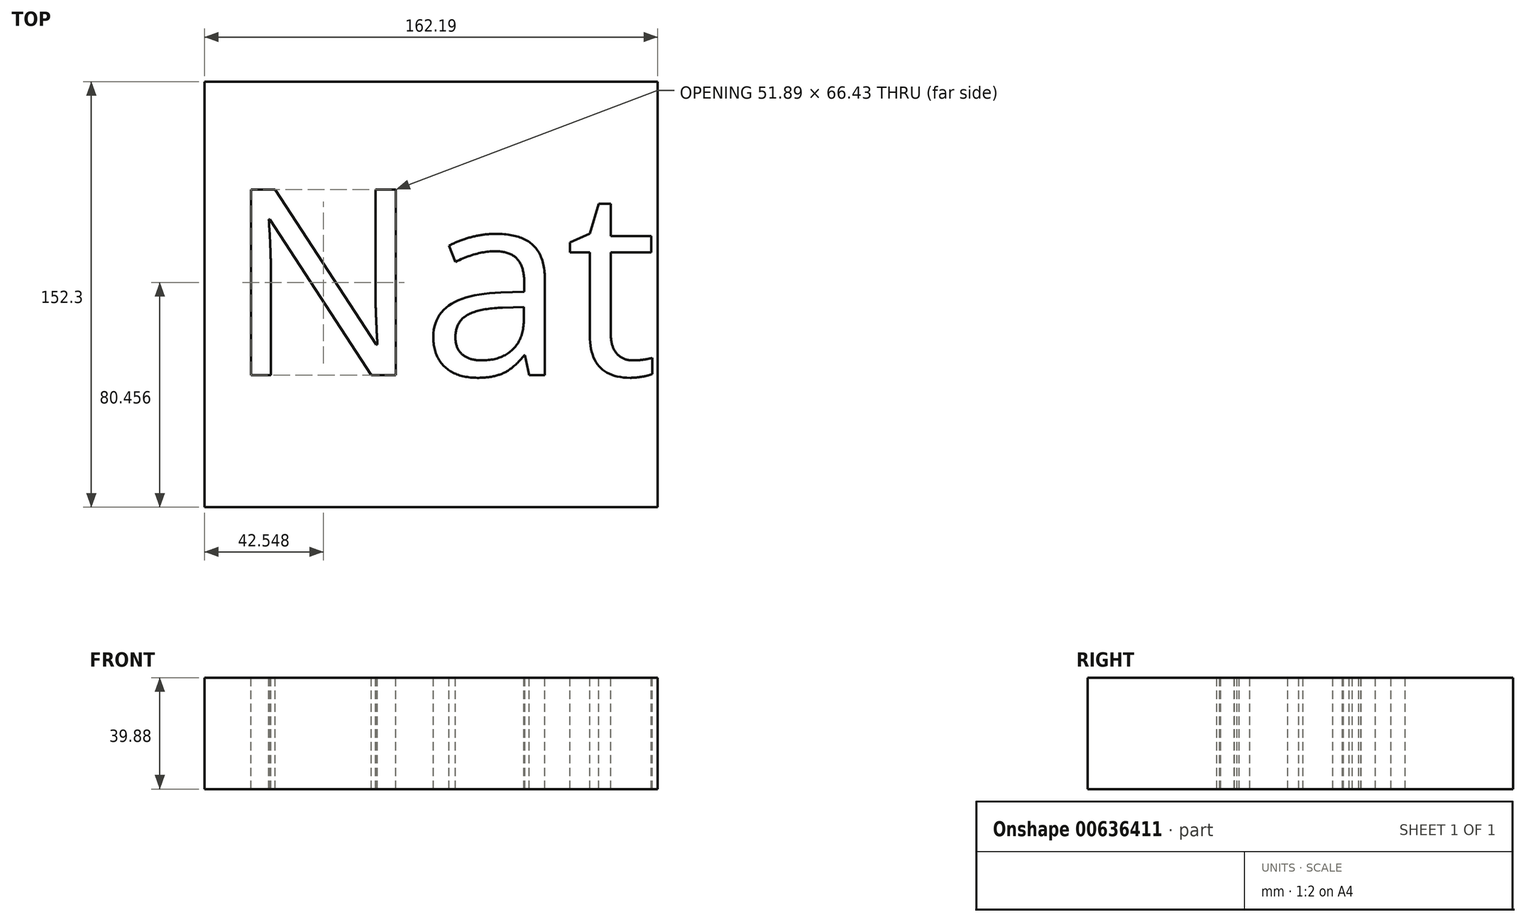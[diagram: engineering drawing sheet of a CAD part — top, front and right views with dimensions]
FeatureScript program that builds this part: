
annotation { "Feature Type Name" : "Feature", "Feature Type Description" : "" }
export const myFeature = defineFeature(function(context is Context, id is Id, definition is map)
    precondition{}
    {
        {
            var Q0;
            Q0=qCreatedBy(makeId("Top.planeOp"),FACE);
            var sketch = newSketch(context, id + "F0", { "sketchPlane" : qUnion([Q0])});
            skLineSegment(sketch, "E0.bottom", {"start": v(-82.54, 73.86) * mm, "end": v(79.65, 73.86) * mm});
            skLineSegment(sketch, "E0.top", {"start": v(-82.54, -78.44) * mm, "end": v(79.65, -78.44) * mm});
            skLineSegment(sketch, "E0.left", {"start": v(-82.54, 73.86) * mm, "end": v(-82.54, -78.44) * mm});
            skLineSegment(sketch, "E0.right", {"start": v(79.65, 73.86) * mm, "end": v(79.65, -78.44) * mm});
            skSolve(sketch);
        }
        {
            var Q0;
            Q0 = qSketchRegion(id + "F0", true);
            extrude(context, id + "F1", {"entities" : qUnion([Q0]), "depth" : 39.88 * mm, "offsetDistance" : 25.4 * mm});
        }
        {
            var Q0;
            Q0=makeQuery(id+"F1.opExtrude","CAP_FACE",FACE,{"disambiguationData":[OSD([sQuery(id+"F0.wireOp",EDGE,"E0.bottom"),sQuery(id+"F0.wireOp",EDGE,"E0.top"),sQuery(id+"F0.wireOp",EDGE,"E0.left"),sQuery(id+"F0.wireOp",EDGE,"E0.right")])],"isStart":false});
            var sketch = newSketch(context, id + "F2", { "sketchPlane" : qUnion([Q0])});
            skText(sketch, "E1", { "text": "Natneut", "fontName": "OpenSans-Regular.ttf"});
            const initialGuessF2  = {"E1": [-0.07507, -0.0312, 1, 0, 0.067]};
            skSetInitialGuess(sketch, initialGuessF2);
            skSolve(sketch);
        }
        {
            var Q0;
            Q0 = qSketchRegion(id + "F2", true);
            extrude(context, id + "F3", {"entities" : qUnion([Q0]), "operationType" : NewBodyOperationType.REMOVE, "oppositeDirection" : true, "depth" : 80.52 * mm, "offsetDistance" : 25.4 * mm});
        }
    });
